# Revit family: 34. Секция фильтрования, вод. нагр. и вент. выброс прямо и резервным эл.двигателем ANR A1 REZ
name_source: partatom
category: Оборудование
revit_build: Autodesk Revit 2016 (Build: 20161004_0715(x64)
units: mm (PartAtom-declared; Revit-internal decimal feet)

## family parameters
Всегда вертикально = Да
На основе рабочей плоскости = Нет
Общий = Нет
При загрузке вырезать с полостями = Нет
Размер круглого соединителя = Использовать диаметр
Тип детали = Нормальный
Точка расчета площади = Нет

## types (4) — shared parameters
h = 130 мм
Г = 85 мм
Д = 2150 мм
Д1 = 2130 мм
Д2 = 533 мм
Д3 = 266 мм
Единица измерения = шт.
Завод изготовитель = KORF
Ключевая пометка = Вентиляция
Материал = Сталь серая
Наименование и тех.хар-ка = Секция фильтрования EU4, водяного нагрева вместе с вентилятором выброс прямо и резервным эл.двигателем
Раздел = ОВ
Синий = Синий
высота ножек = 120 мм

## per-type parameters (varying)
| type | d | А | А1 | Б | Б1 | Высота | Размер В | Середина | Ширина |
| ANR 6 A1 REZ | 32 мм | 1100 мм | 1080 мм | 1100 мм | 1080 мм | 1025 мм | 735 мм | 670 мм | 1025 мм |
| ANR 7 A1 REZ | 38 мм | 1100 мм | 1080 мм | 1320 мм | 1300 мм | 1245 мм | 985 мм | 780 мм | 1025 мм |
| ANR 8 A1 REZ | 38 мм | 1320 мм | 1300 мм | 1320 мм | 1300 мм | 1245 мм | 985 мм | 780 мм | 1245 мм |
| ANR 12 A1 REZ | 51 мм | 1435 мм | 1415 мм | 1435 мм | 1415 мм | 1360 мм | 1060 мм | 838 мм | 1360 мм |

note: column(s) folded — value = type name in every type: Тип, марка, обозначение
